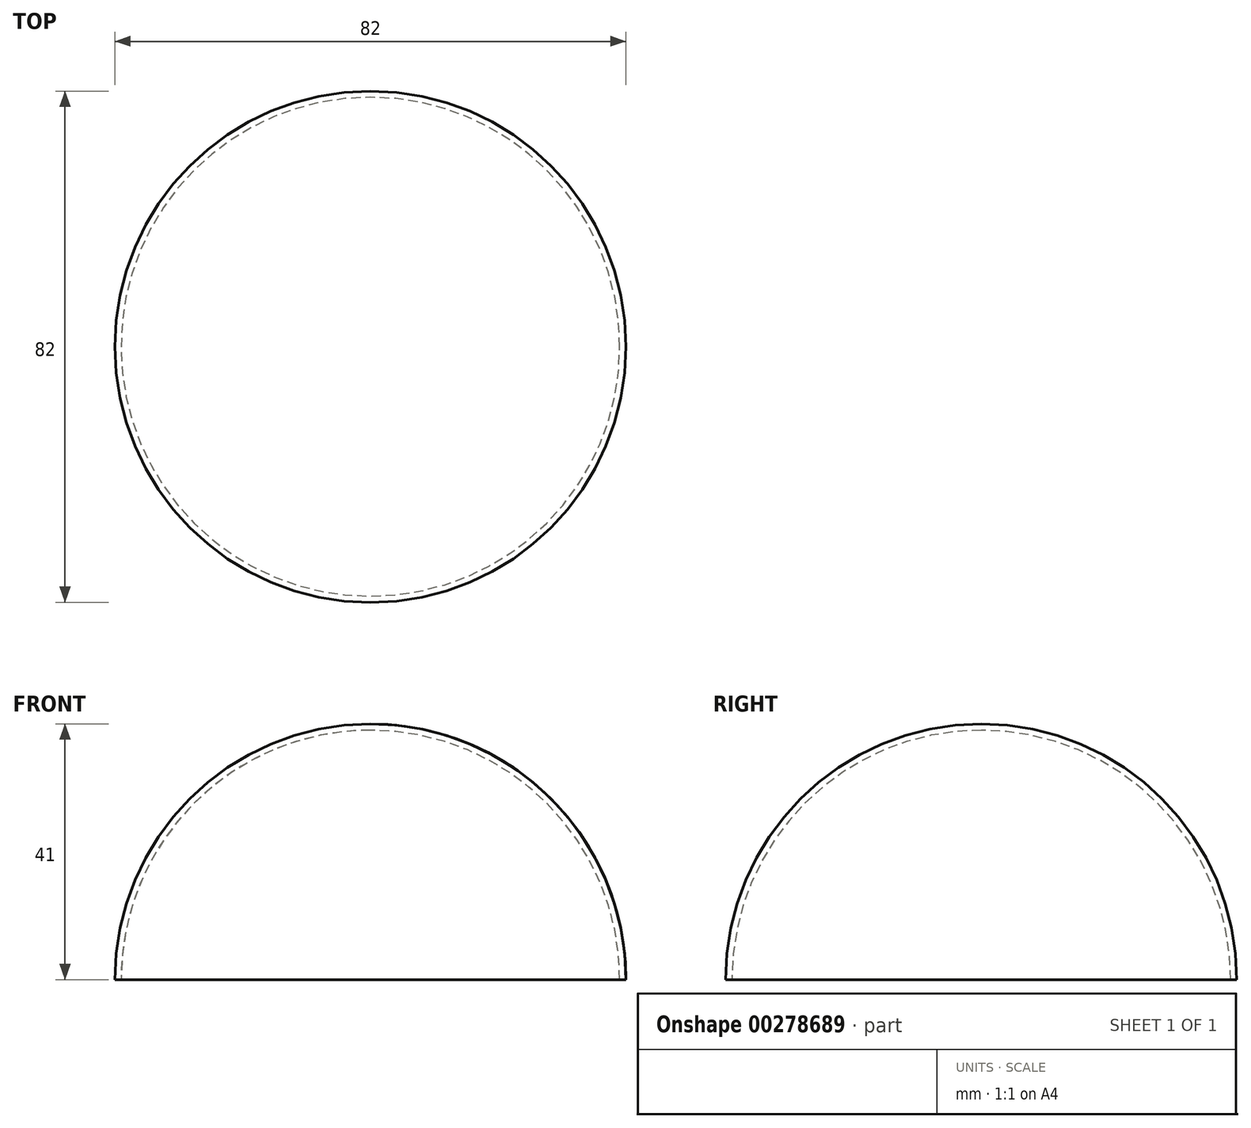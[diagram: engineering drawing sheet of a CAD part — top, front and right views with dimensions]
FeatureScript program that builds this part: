
annotation { "Feature Type Name" : "Feature", "Feature Type Description" : "" }
export const myFeature = defineFeature(function(context is Context, id is Id, definition is map)
    precondition{}
    {
        {
            var Q0;
            Q0=qCreatedBy(makeId("Front.planeOp"),FACE);
            var sketch = newSketch(context, id + "F0", { "sketchPlane" : qUnion([Q0])});
            skArc(sketch, "E0", {"start": v(0, 40) * mm, "mid": v(-28.28, 28.28) * mm, "end": v(-40, 0) * mm});
            skArc(sketch, "E1.0", {"start": v(0, 41) * mm, "mid": v(-29, 29) * mm, "end": v(-41, 0) * mm});
            skLineSegment(sketch, "E2", {"start": v(0, 0) * mm, "end": v(-41, 0) * mm});
            skLineSegment(sketch, "E3", {"start": v(0, 0) * mm, "end": v(0, 41) * mm});
            skSolve(sketch);
        }
        {
            var Q0;
            {var subQ0=sQuery(id+"F0.wireOp",EDGE,"E0");Q0=makeQuery(id+"F0.imprint","IMPRINT",FACE,{"disambiguationData":[TD([[makeQuery(id+"F0.imprint","IMPRINT",EDGE,{"derivedFrom":subQ0}),-1.0]])]});}
            var Q1;
            Q1=sQuery(id+"F0.wireOp",EDGE,"E3");
            revolve(context, id + "F1", {"entities" : qUnion([Q0]), "axis" : qUnion([Q1]), "revolveType" : RevolveType.FULL});
        }
    });
